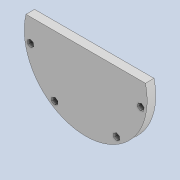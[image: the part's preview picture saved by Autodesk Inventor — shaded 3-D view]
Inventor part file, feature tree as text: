
AUTODESK INVENTOR PART (.ipt)
format: ipt  version: 2020.4 (Build 244396000, 396)  size: 115,200 bytes
history: native  units: mm
features: extrude x1, sketch x1
ambient origin geometry x8: Origin, YZ Plane, XZ Plane, XY Plane, X Axis, Y Axis, Z Axis, Center Point
bodies: Solid1 (feature_tree)
feature tree (2):
  extrude  "Extrusion1"  Depth=12.0mm
  sketch  "Sketch1"  dims[d0=171.6mm d1=78.0mm d2=78.0mm d5=12.0mm d6=4.22mm d7=4.22mm d10=12.0mm d11=20.0mm d13=8.290314mm d15=20.0mm d17=8.290314mm d19=20.0mm d20=12.0mm d21=0.0mm]
